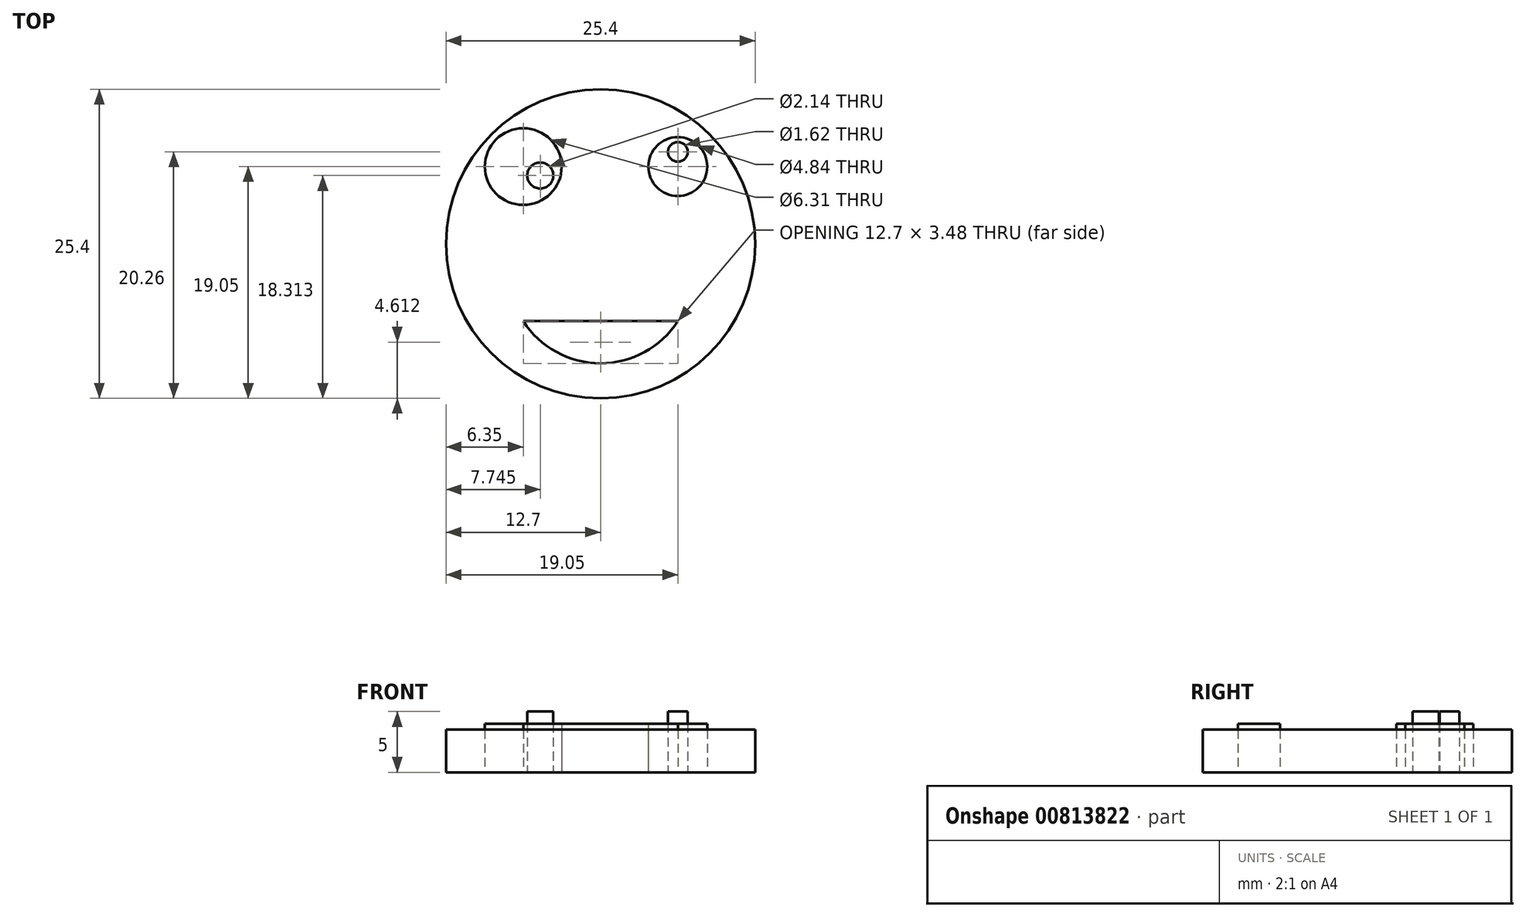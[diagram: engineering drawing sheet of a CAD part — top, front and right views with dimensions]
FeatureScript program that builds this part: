
annotation { "Feature Type Name" : "Feature", "Feature Type Description" : "" }
export const myFeature = defineFeature(function(context is Context, id is Id, definition is map)
    precondition{}
    {
        {
            var Q0;
            Q0=qCreatedBy(makeId("Top.planeOp"),FACE);
            var sketch = newSketch(context, id + "F0", { "sketchPlane" : qUnion([Q0])});
            skCircle(sketch, "E0", {"center": v(0, 0) * mm, "radius": 12.7 * mm});
            skCircle(sketch, "E1", {"center": v(6.35, 6.35) * mm, "radius": 2.42 * mm});
            skCircle(sketch, "E2", {"center": v(-6.35, 6.35) * mm, "radius": 3.16 * mm});
            skArc(sketch, "E3", {"start": v(-6.35, -6.35) * mm, "mid": v(0, -9.83) * mm, "end": v(6.35, -6.35) * mm});
            skLineSegment(sketch, "E4", {"start": v(6.35, -6.35) * mm, "end": v(-6.35, -6.35) * mm});
            skCircle(sketch, "E5", {"center": v(-4.95, 5.61) * mm, "radius": 1.07 * mm});
            skCircle(sketch, "E6", {"center": v(6.35, 7.56) * mm, "radius": 0.8 * mm});
            skSolve(sketch);
        }
        {
            var Q0;
            Q0=makeQuery(id+"F0.imprint","IMPRINT",FACE,{"disambiguationData":[TD([[makeQuery(id+"F0.imprint","IMPRINT",EDGE,{"derivedFrom":sQuery(id+"F0.wireOp",EDGE,"E5")}),1.0]])]});
            var Q1;
            Q1=makeQuery(id+"F0.imprint","IMPRINT",FACE,{"disambiguationData":[TD([[makeQuery(id+"F0.imprint","IMPRINT",EDGE,{"derivedFrom":sQuery(id+"F0.wireOp",EDGE,"E6")}),1.0]])]});
            extrude(context, id + "F1", {"entities" : qUnion([Q0, Q1]), "depth" : 5 * mm, "offsetDistance" : 25.4 * mm});
        }
        {
            var Q0;
            Q0=makeQuery(id+"F0.imprint","IMPRINT",FACE,{"disambiguationData":[TD([[makeQuery(id+"F0.imprint","IMPRINT",EDGE,{"derivedFrom":sQuery(id+"F0.wireOp",EDGE,"E2")}),1.0]])]});
            var Q1;
            Q1=makeQuery(id+"F0.imprint","IMPRINT",FACE,{"disambiguationData":[TD([[makeQuery(id+"F0.imprint","IMPRINT",EDGE,{"derivedFrom":sQuery(id+"F0.wireOp",EDGE,"E1")}),1.0]])]});
            var Q2;
            Q2=makeQuery(id+"F0.imprint","IMPRINT",FACE,{"disambiguationData":[TD([[makeQuery(id+"F0.imprint","IMPRINT",EDGE,{"derivedFrom":sQuery(id+"F0.wireOp",EDGE,"E3")}),1.0]])]});
            extrude(context, id + "F2", {"entities" : qUnion([Q0, Q1, Q2]), "depth" : 4 * mm, "offsetDistance" : 25.4 * mm});
        }
        {
            var Q0;
            Q0=makeQuery(id+"F0.imprint","IMPRINT",FACE,{"disambiguationData":[TD([[makeQuery(id+"F0.imprint","IMPRINT",EDGE,{"derivedFrom":sQuery(id+"F0.wireOp",EDGE,"E0")}),1.0]])]});
            extrude(context, id + "F3", {"entities" : qUnion([Q0]), "depth" : 3.5 * mm, "offsetDistance" : 25.4 * mm});
        }
    });
